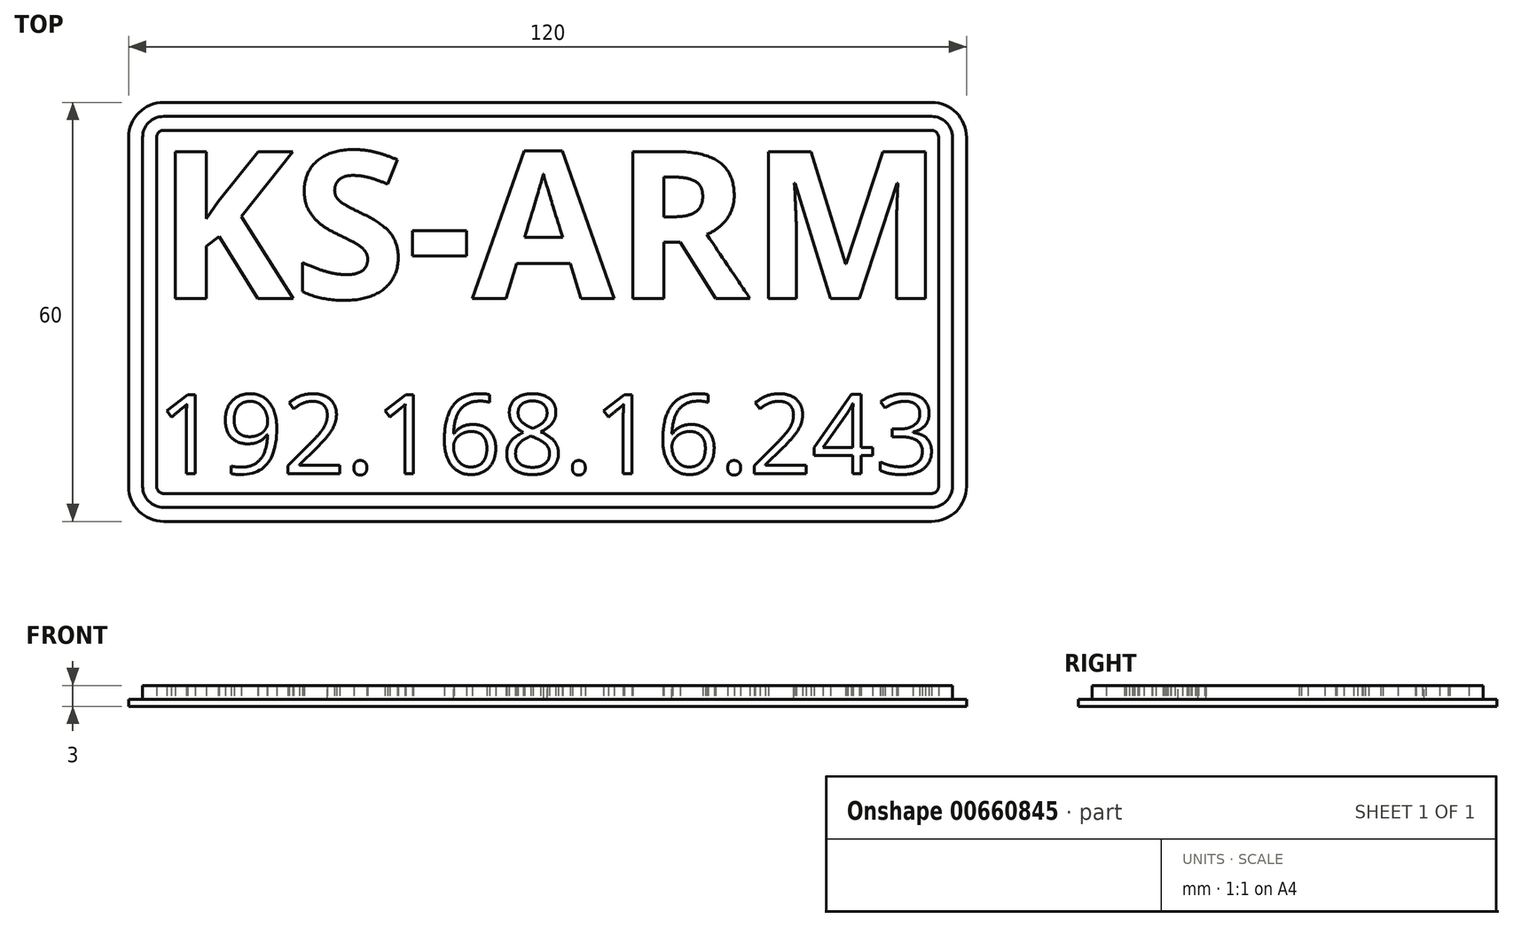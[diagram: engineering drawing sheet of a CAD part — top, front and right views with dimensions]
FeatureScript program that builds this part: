
annotation { "Feature Type Name" : "Feature", "Feature Type Description" : "" }
export const myFeature = defineFeature(function(context is Context, id is Id, definition is map)
    precondition{}
    {
        {
            assignVariable(context, id + "F0", {"variableType" : VariableType.LENGTH, "name" : "st", "lengthValue" : 1 * mm});
        }
        {
            assignVariable(context, id + "F1", {"variableType" : VariableType.LENGTH, "name" : "ft", "lengthValue" : 2 * mm});
        }
        {
            var Q0;
            Q0=qCreatedBy(makeId("Top.planeOp"),FACE);
            var sketch = newSketch(context, id + "F2", { "sketchPlane" : qUnion([Q0])});
            skLineSegment(sketch, "E0.bottom", {"start": v(-55, 30) * mm, "end": v(55, 30) * mm});
            skLineSegment(sketch, "E0.top", {"start": v(-55, -30) * mm, "end": v(55, -30) * mm});
            skLineSegment(sketch, "E0.left", {"start": v(-60, 25) * mm, "end": v(-60, -25) * mm});
            skLineSegment(sketch, "E0.right", {"start": v(60, 25) * mm, "end": v(60, -25) * mm});
            skPoint(sketch, "E1", {"position": v(0, 30) * mm});
            skPoint(sketch, "E2", {"position": v(-60, 0) * mm});
            skPoint(sketch, "E3.visualSharp", {"position": v(-60, 30) * mm});
            skArc(sketch, "E3.filletArc", {"start": v(-55, 30) * mm, "mid": v(-58.54, 28.54) * mm, "end": v(-60, 25) * mm});
            skPoint(sketch, "E4.visualSharp", {"position": v(60, 30) * mm});
            skArc(sketch, "E4.filletArc", {"start": v(60, 25) * mm, "mid": v(58.54, 28.54) * mm, "end": v(55, 30) * mm});
            skPoint(sketch, "E5.visualSharp", {"position": v(60, -30) * mm});
            skArc(sketch, "E5.filletArc", {"start": v(55, -30) * mm, "mid": v(58.54, -28.54) * mm, "end": v(60, -25) * mm});
            skPoint(sketch, "E6.visualSharp", {"position": v(-60, -30) * mm});
            skArc(sketch, "E6.filletArc", {"start": v(-60, -25) * mm, "mid": v(-58.54, -28.54) * mm, "end": v(-55, -30) * mm});
            skSolve(sketch);
        }
        {
            var Q0;
            Q0 = qSketchRegion(id + "F2", true);
            extrude(context, id + "F3", {"entities" : qUnion([Q0]), "depth" : getVariable(context, 'st'), "offsetDistance" : 25 * mm});
        }
        {
            var Q0;
            Q0=makeQuery(id+"F3.opExtrude","CAP_FACE",FACE,{"disambiguationData":[OSD([sQuery(id+"F2.wireOp",EDGE,"E0.bottom"),sQuery(id+"F2.wireOp",EDGE,"E0.top"),sQuery(id+"F2.wireOp",EDGE,"E0.left"),sQuery(id+"F2.wireOp",EDGE,"E0.right"),sQuery(id+"F2.wireOp",EDGE,"E3.filletArc"),sQuery(id+"F2.wireOp",EDGE,"E4.filletArc"),sQuery(id+"F2.wireOp",EDGE,"E5.filletArc"),sQuery(id+"F2.wireOp",EDGE,"E6.filletArc")])],"isStart":false});
            var sketch = newSketch(context, id + "F4", { "sketchPlane" : qUnion([Q0])});
            skArc(sketch, "E7.0", {"start": v(-55, 28) * mm, "mid": v(-57.12, 27.12) * mm, "end": v(-58, 25) * mm});
            skLineSegment(sketch, "E7.1", {"start": v(-55, 28) * mm, "end": v(55, 28) * mm});
            skLineSegment(sketch, "E7.2", {"start": v(-58, 25) * mm, "end": v(-58, -25) * mm});
            skArc(sketch, "E7.3", {"start": v(58, 25) * mm, "mid": v(57.12, 27.12) * mm, "end": v(55, 28) * mm});
            skArc(sketch, "E7.4", {"start": v(-58, -25) * mm, "mid": v(-57.12, -27.12) * mm, "end": v(-55, -28) * mm});
            skLineSegment(sketch, "E7.5", {"start": v(-55, -28) * mm, "end": v(55, -28) * mm});
            skArc(sketch, "E7.6", {"start": v(55, -28) * mm, "mid": v(57.12, -27.12) * mm, "end": v(58, -25) * mm});
            skLineSegment(sketch, "E7.7", {"start": v(58, 25) * mm, "end": v(58, -25) * mm});
            skArc(sketch, "E8.0", {"start": v(-55, 26) * mm, "mid": v(-55.7, 25.7) * mm, "end": v(-56, 25) * mm});
            skLineSegment(sketch, "E8.1", {"start": v(-55, 26) * mm, "end": v(55, 26) * mm});
            skLineSegment(sketch, "E8.2", {"start": v(-56, 25) * mm, "end": v(-56, -25) * mm});
            skArc(sketch, "E8.3", {"start": v(56, 25) * mm, "mid": v(55.7, 25.7) * mm, "end": v(55, 26) * mm});
            skArc(sketch, "E8.4", {"start": v(-56, -25) * mm, "mid": v(-55.7, -25.7) * mm, "end": v(-55, -26) * mm});
            skLineSegment(sketch, "E8.5", {"start": v(-55, -26) * mm, "end": v(55, -26) * mm});
            skArc(sketch, "E8.6", {"start": v(55, -26) * mm, "mid": v(55.7, -25.7) * mm, "end": v(56, -25) * mm});
            skLineSegment(sketch, "E8.7", {"start": v(56, 25) * mm, "end": v(56, -25) * mm});
            skText(sketch, "E9", { "text": "KS-ARM", "fontName": "OpenSans-Bold.ttf"});
            skText(sketch, "E10", { "text": "192.168.16.243", "fontName": "OpenSans-Regular.ttf"});
            skLineSegment(sketch, "E11", {"start": v(0, -23.14) * mm, "end": v(0, 23.14) * mm, "construction": true});
            const initialGuessF4  = {"E9": [-0.056, 0.00194, 1, 0, 0.0212], "E10": [-0.056, -0.02314, 1, 0, 0.01137]};
            skSetInitialGuess(sketch, initialGuessF4);
            skSolve(sketch);
        }
        {
            var Q0;
            Q0=makeQuery(id+"F4.imprint","IMPRINT",FACE,{"disambiguationData":[TD([[makeQuery(id+"F4.imprint","IMPRINT",EDGE,{"derivedFrom":sQuery(id+"F4.wireOp",EDGE,"E10.sketch_text.stroke-215")}),-1.0]])]});
            var Q1;
            Q1=makeQuery(id+"F4.imprint","IMPRINT",FACE,{"disambiguationData":[TD([[makeQuery(id+"F4.imprint","IMPRINT",EDGE,{"derivedFrom":sQuery(id+"F4.wireOp",EDGE,"E10.sketch_text.stroke-198")}),-1.0]])]});
            var Q2;
            Q2=makeQuery(id+"F4.imprint","IMPRINT",FACE,{"disambiguationData":[TD([[makeQuery(id+"F4.imprint","IMPRINT",EDGE,{"derivedFrom":sQuery(id+"F4.wireOp",EDGE,"E10.sketch_text.stroke-178")}),-1.0]])]});
            var Q3;
            Q3=makeQuery(id+"F4.imprint","IMPRINT",FACE,{"disambiguationData":[TD([[makeQuery(id+"F4.imprint","IMPRINT",EDGE,{"derivedFrom":sQuery(id+"F4.wireOp",EDGE,"E10.sketch_text.stroke-170")}),-1.0]])]});
            var Q4;
            Q4=makeQuery(id+"F4.imprint","IMPRINT",FACE,{"disambiguationData":[TD([[makeQuery(id+"F4.imprint","IMPRINT",EDGE,{"derivedFrom":sQuery(id+"F4.wireOp",EDGE,"E10.sketch_text.stroke-145")}),-1.0]])]});
            var Q5;
            Q5=makeQuery(id+"F4.imprint","IMPRINT",FACE,{"disambiguationData":[TD([[makeQuery(id+"F4.imprint","IMPRINT",EDGE,{"derivedFrom":sQuery(id+"F4.wireOp",EDGE,"E10.sketch_text.stroke-136")}),-1.0]])]});
            var Q6;
            Q6=makeQuery(id+"F4.imprint","IMPRINT",FACE,{"disambiguationData":[TD([[makeQuery(id+"F4.imprint","IMPRINT",EDGE,{"derivedFrom":sQuery(id+"F4.wireOp",EDGE,"E10.sketch_text.stroke-128")}),-1.0]])]});
            var Q7;
            Q7=makeQuery(id+"F4.imprint","IMPRINT",FACE,{"disambiguationData":[TD([[makeQuery(id+"F4.imprint","IMPRINT",EDGE,{"derivedFrom":sQuery(id+"F4.wireOp",EDGE,"E10.sketch_text.stroke-97")}),-1.0]])]});
            var Q8;
            Q8=makeQuery(id+"F4.imprint","IMPRINT",FACE,{"disambiguationData":[TD([[makeQuery(id+"F4.imprint","IMPRINT",EDGE,{"derivedFrom":sQuery(id+"F4.wireOp",EDGE,"E10.sketch_text.stroke-72")}),-1.0]])]});
            var Q9;
            Q9=makeQuery(id+"F4.imprint","IMPRINT",FACE,{"disambiguationData":[TD([[makeQuery(id+"F4.imprint","IMPRINT",EDGE,{"derivedFrom":sQuery(id+"F4.wireOp",EDGE,"E10.sketch_text.stroke-0")}),-1.0]])]});
            var Q10;
            Q10=makeQuery(id+"F4.imprint","IMPRINT",FACE,{"disambiguationData":[TD([[makeQuery(id+"F4.imprint","IMPRINT",EDGE,{"derivedFrom":sQuery(id+"F4.wireOp",EDGE,"E10.sketch_text.stroke-9")}),-1.0]])]});
            var Q11;
            Q11=makeQuery(id+"F4.imprint","IMPRINT",FACE,{"disambiguationData":[TD([[makeQuery(id+"F4.imprint","IMPRINT",EDGE,{"derivedFrom":sQuery(id+"F4.wireOp",EDGE,"E10.sketch_text.stroke-35")}),-1.0]])]});
            var Q12;
            Q12=makeQuery(id+"F4.imprint","IMPRINT",FACE,{"disambiguationData":[TD([[makeQuery(id+"F4.imprint","IMPRINT",EDGE,{"derivedFrom":sQuery(id+"F4.wireOp",EDGE,"E10.sketch_text.stroke-55")}),-1.0]])]});
            var Q13;
            Q13=makeQuery(id+"F4.imprint","IMPRINT",FACE,{"disambiguationData":[TD([[makeQuery(id+"F4.imprint","IMPRINT",EDGE,{"derivedFrom":sQuery(id+"F4.wireOp",EDGE,"E10.sketch_text.stroke-63")}),-1.0]])]});
            var Q14;
            Q14=makeQuery(id+"F4.imprint","IMPRINT",FACE,{"disambiguationData":[TD([[makeQuery(id+"F4.imprint","IMPRINT",EDGE,{"derivedFrom":sQuery(id+"F4.wireOp",EDGE,"E9.sketch_text.stroke-0")}),-1.0]])]});
            var Q15;
            Q15=makeQuery(id+"F4.imprint","IMPRINT",FACE,{"disambiguationData":[TD([[makeQuery(id+"F4.imprint","IMPRINT",EDGE,{"derivedFrom":sQuery(id+"F4.wireOp",EDGE,"E7.0")}),1.0]])]});
            var Q16;
            Q16=makeQuery(id+"F4.imprint","IMPRINT",FACE,{"disambiguationData":[TD([[makeQuery(id+"F4.imprint","IMPRINT",EDGE,{"derivedFrom":sQuery(id+"F4.wireOp",EDGE,"E9.sketch_text.stroke-13")}),-1.0]])]});
            var Q17;
            Q17=makeQuery(id+"F4.imprint","IMPRINT",FACE,{"disambiguationData":[TD([[makeQuery(id+"F4.imprint","IMPRINT",EDGE,{"derivedFrom":sQuery(id+"F4.wireOp",EDGE,"E9.sketch_text.stroke-41")}),-1.0]])]});
            var Q18;
            Q18=makeQuery(id+"F4.imprint","IMPRINT",FACE,{"disambiguationData":[TD([[makeQuery(id+"F4.imprint","IMPRINT",EDGE,{"derivedFrom":sQuery(id+"F4.wireOp",EDGE,"E9.sketch_text.stroke-45")}),-1.0]])]});
            var Q19;
            Q19=makeQuery(id+"F4.imprint","IMPRINT",FACE,{"disambiguationData":[TD([[makeQuery(id+"F4.imprint","IMPRINT",EDGE,{"derivedFrom":sQuery(id+"F4.wireOp",EDGE,"E9.sketch_text.stroke-57")}),-1.0]])]});
            var Q20;
            Q20=makeQuery(id+"F4.imprint","IMPRINT",FACE,{"disambiguationData":[TD([[makeQuery(id+"F4.imprint","IMPRINT",EDGE,{"derivedFrom":sQuery(id+"F4.wireOp",EDGE,"E9.sketch_text.stroke-76")}),-1.0]])]});
            extrude(context, id + "F5", {"entities" : qUnion([Q0, Q1, Q2, Q3, Q4, Q5, Q6, Q7, Q8, Q9, Q10, Q11, Q12, Q13, Q14, Q15, Q16, Q17, Q18, Q19, Q20]), "operationType" : NewBodyOperationType.ADD, "depth" : getVariable(context, 'ft'), "offsetDistance" : 25 * mm});
        }
    });
